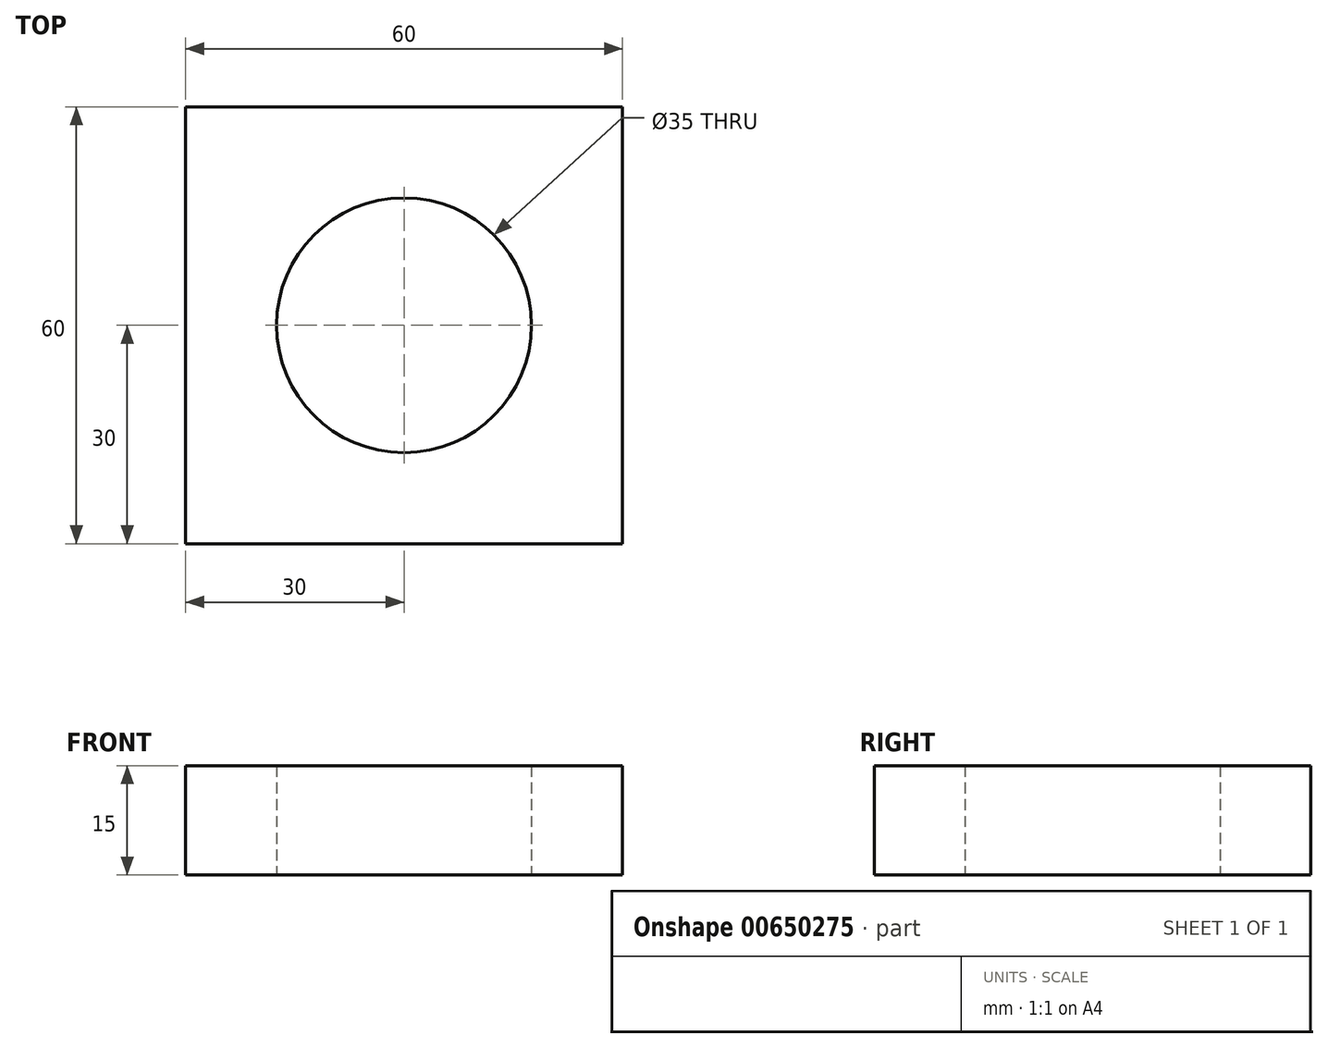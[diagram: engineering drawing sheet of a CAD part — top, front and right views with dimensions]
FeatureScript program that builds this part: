
annotation { "Feature Type Name" : "Feature", "Feature Type Description" : "" }
export const myFeature = defineFeature(function(context is Context, id is Id, definition is map)
    precondition{}
    {
        {
            var Q0;
            Q0=qCreatedBy(makeId("Top.planeOp"),FACE);
            var sketch = newSketch(context, id + "F0", { "sketchPlane" : qUnion([Q0])});
            skCircle(sketch, "E0", {"center": v(0, 0) * mm, "radius": 17.5 * mm});
            skLineSegment(sketch, "E1.bottom", {"start": v(30, -30) * mm, "end": v(-30, -30) * mm});
            skLineSegment(sketch, "E1.top", {"start": v(30, 30) * mm, "end": v(-30, 30) * mm});
            skLineSegment(sketch, "E1.left", {"start": v(30, -30) * mm, "end": v(30, 30) * mm});
            skLineSegment(sketch, "E1.right", {"start": v(-30, -30) * mm, "end": v(-30, 30) * mm});
            skSolve(sketch);
        }
        {
            var Q0;
            Q0=makeQuery(id+"F0.imprint","IMPRINT",FACE,{"disambiguationData":[TD([[makeQuery(id+"F0.imprint","IMPRINT",EDGE,{"derivedFrom":sQuery(id+"F0.wireOp",EDGE,"E0")}),-1.0]])]});
            extrude(context, id + "F1", {"entities" : qUnion([Q0]), "depth" : 15 * mm, "offsetDistance" : 25 * mm});
        }
    });
